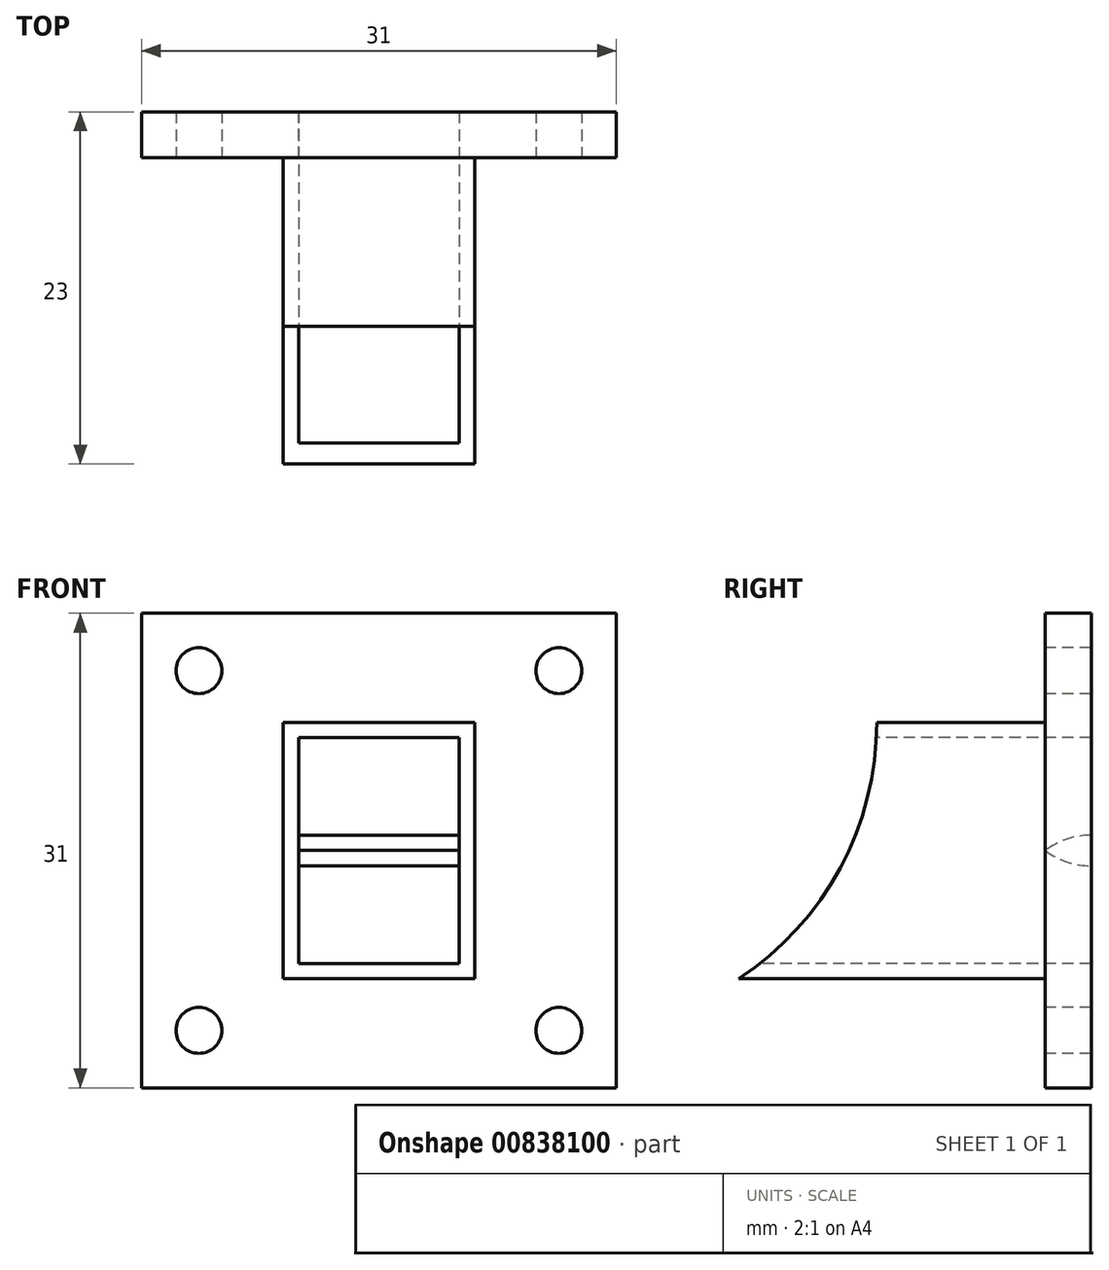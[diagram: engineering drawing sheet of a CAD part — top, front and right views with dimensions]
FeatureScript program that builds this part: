
annotation { "Feature Type Name" : "Feature", "Feature Type Description" : "" }
export const myFeature = defineFeature(function(context is Context, id is Id, definition is map)
    precondition{}
    {
        {
            var Q0;
            Q0=qCreatedBy(makeId("Front.planeOp"),FACE);
            var sketch = newSketch(context, id + "F0", { "sketchPlane" : qUnion([Q0])});
            skLineSegment(sketch, "E0.bottom", {"start": v(15.5, -15.5) * mm, "end": v(-15.5, -15.5) * mm});
            skLineSegment(sketch, "E0.top", {"start": v(15.5, 15.5) * mm, "end": v(-15.5, 15.5) * mm});
            skLineSegment(sketch, "E0.left", {"start": v(15.5, -15.5) * mm, "end": v(15.5, 15.5) * mm});
            skLineSegment(sketch, "E0.right", {"start": v(-15.5, -15.5) * mm, "end": v(-15.5, 15.5) * mm});
            skPoint(sketch, "E0.middle", {"position": v(0, 0) * mm});
            skSolve(sketch);
        }
        {
            var Q0;
            Q0 = qSketchRegion(id + "F0", true);
            extrude(context, id + "F1", {"entities" : qUnion([Q0]), "depth" : 3 * mm, "offsetDistance" : 25 * mm});
        }
        {
            var Q0;
            Q0=makeQuery(id+"F1.opExtrude","CAP_FACE",FACE,{"disambiguationData":[OSD([sQuery(id+"F0.wireOp",EDGE,"E0.bottom"),sQuery(id+"F0.wireOp",EDGE,"E0.top"),sQuery(id+"F0.wireOp",EDGE,"E0.left"),sQuery(id+"F0.wireOp",EDGE,"E0.right")])],"isStart":false});
            var sketch = newSketch(context, id + "F2", { "sketchPlane" : qUnion([Q0])});
            skCircle(sketch, "E1", {"center": v(-11.75, -11.75) * mm, "radius": 1.5 * mm});
            skCircle(sketch, "E2", {"center": v(-11.75, 11.75) * mm, "radius": 1.5 * mm});
            skCircle(sketch, "E3", {"center": v(11.75, 11.75) * mm, "radius": 1.5 * mm});
            skCircle(sketch, "E4", {"center": v(11.75, -11.75) * mm, "radius": 1.5 * mm});
            skLineSegment(sketch, "E5", {"start": v(-11.75, -11.75) * mm, "end": v(11.75, -11.75) * mm, "construction": true});
            skLineSegment(sketch, "E6", {"start": v(-11.75, 11.75) * mm, "end": v(-11.75, -11.75) * mm, "construction": true});
            skSolve(sketch);
        }
        {
            var Q0;
            Q0 = qSketchRegion(id + "F2", true);
            extrude(context, id + "F3", {"entities" : qUnion([Q0]), "operationType" : NewBodyOperationType.REMOVE, "oppositeDirection" : true, "depth" : 3 * mm, "offsetDistance" : 25 * mm});
        }
        {
            var Q0;
            Q0=makeQuery(id+"F1.opExtrude","CAP_FACE",FACE,{"disambiguationData":[OSD([sQuery(id+"F0.wireOp",EDGE,"E0.bottom"),sQuery(id+"F0.wireOp",EDGE,"E0.top"),sQuery(id+"F0.wireOp",EDGE,"E0.left"),sQuery(id+"F0.wireOp",EDGE,"E0.right")])],"isStart":false});
            var sketch = newSketch(context, id + "F4", { "sketchPlane" : qUnion([Q0])});
            skLineSegment(sketch, "E7.bottom", {"start": v(6.25, -8.37) * mm, "end": v(-6.25, -8.38) * mm});
            skLineSegment(sketch, "E7.top", {"start": v(6.25, 8.38) * mm, "end": v(-6.25, 8.38) * mm});
            skLineSegment(sketch, "E7.left", {"start": v(6.25, -8.37) * mm, "end": v(6.25, 8.38) * mm});
            skLineSegment(sketch, "E7.right", {"start": v(-6.25, -8.38) * mm, "end": v(-6.25, 8.38) * mm});
            skPoint(sketch, "E7.middle", {"position": v(0, 0) * mm});
            skSolve(sketch);
        }
        {
            var Q0;
            Q0 = qSketchRegion(id + "F4", true);
            extrude(context, id + "F5", {"entities" : qUnion([Q0]), "operationType" : NewBodyOperationType.ADD, "depth" : 20 * mm, "offsetDistance" : 25 * mm});
        }
        {
            var Q0;
            Q0=makeQuery(id+"F5.opExtrude","CAP_FACE",FACE,{"disambiguationData":[OSD([sQuery(id+"F4.wireOp",EDGE,"E7.bottom"),sQuery(id+"F4.wireOp",EDGE,"E7.top"),sQuery(id+"F4.wireOp",EDGE,"E7.left"),sQuery(id+"F4.wireOp",EDGE,"E7.right")])],"isStart":false});
            var sketch = newSketch(context, id + "F6", { "sketchPlane" : qUnion([Q0])});
            skLineSegment(sketch, "E8.bottom", {"start": v(5.25, -7.37) * mm, "end": v(-5.25, -7.38) * mm});
            skLineSegment(sketch, "E8.top", {"start": v(5.25, 7.38) * mm, "end": v(-5.25, 7.38) * mm});
            skLineSegment(sketch, "E8.left", {"start": v(5.25, -7.38) * mm, "end": v(5.25, 7.38) * mm});
            skLineSegment(sketch, "E8.right", {"start": v(-5.25, -7.38) * mm, "end": v(-5.25, 7.38) * mm});
            skPoint(sketch, "E8.middle", {"position": v(0, 0) * mm});
            skSolve(sketch);
        }
        {
            var Q0;
            Q0 = qSketchRegion(id + "F6", true);
            extrude(context, id + "F7", {"entities" : qUnion([Q0]), "operationType" : NewBodyOperationType.REMOVE, "oppositeDirection" : true, "depth" : 23 * mm, "offsetDistance" : 25 * mm});
        }
        {
            var Q0;
            Q0=makeQuery(id+"F5.opExtrude","SWEPT_FACE",FACE,{"disambiguationData":[OSD([sQuery(id+"F4.wireOp",EDGE,"E7.left")])]});
            var sketch = newSketch(context, id + "F8", { "sketchPlane" : qUnion([Q0])});
            skCircle(sketch, "E9", {"center": v(-34, 8.33) * mm, "radius": 20 * mm});
            skPoint(sketch, "E10", {"position": v(-23, -8.37) * mm});
            skSolve(sketch);
        }
        {
            var Q0;
            Q0 = qSketchRegion(id + "F8", true);
            extrude(context, id + "F9", {"entities" : qUnion([Q0]), "operationType" : NewBodyOperationType.REMOVE, "oppositeDirection" : true, "depth" : 25 * mm, "offsetDistance" : 25 * mm});
        }
        {
            var Q0;
            Q0=makeQuery(id+"F1.opExtrude","CAP_FACE",FACE,{"disambiguationData":[OSD([sQuery(id+"F0.wireOp",EDGE,"E0.bottom"),sQuery(id+"F0.wireOp",EDGE,"E0.top"),sQuery(id+"F0.wireOp",EDGE,"E0.left"),sQuery(id+"F0.wireOp",EDGE,"E0.right")])],"isStart":false});
            var sketch = newSketch(context, id + "F10", { "sketchPlane" : qUnion([Q0])});
            skLineSegment(sketch, "E11.bottom", {"start": v(6.25, -1) * mm, "end": v(-6.25, -1) * mm});
            skLineSegment(sketch, "E11.top", {"start": v(6.25, 0) * mm, "end": v(-6.25, 0) * mm});
            skLineSegment(sketch, "E11.left", {"start": v(6.25, -1) * mm, "end": v(6.25, 0) * mm});
            skLineSegment(sketch, "E11.right", {"start": v(-6.25, -1) * mm, "end": v(-6.25, 0) * mm});
            skPoint(sketch, "E11.middle", {"position": v(0, -0.5) * mm});
            skSolve(sketch);
        }
        {
            var Q0;
            Q0 = qSketchRegion(id + "F10", true);
            extrude(context, id + "F11", {"entities" : qUnion([Q0]), "operationType" : NewBodyOperationType.ADD, "oppositeDirection" : true, "depth" : 3 * mm, "offsetDistance" : 25 * mm});
        }
        {
            var Q0;
            Q0=makeQuery(id+"F11.opExtrude","CAP_EDGE",EDGE,{"disambiguationData":[OSD([sQuery(id+"F10.wireOp",EDGE,"E11.bottom")])],"isStart":true});
            fillet(context, id + "F12", {"entities" : qUnion([Q0]), "radius" : 5 * mm, "tangentPropagation" : true, "allowEdgeOverflow" : false});
        }
        {
            var Q0;
            Q0=makeQuery(id+"F1.opExtrude","CAP_FACE",FACE,{"disambiguationData":[OSD([sQuery(id+"F0.wireOp",EDGE,"E0.bottom"),sQuery(id+"F0.wireOp",EDGE,"E0.top"),sQuery(id+"F0.wireOp",EDGE,"E0.left"),sQuery(id+"F0.wireOp",EDGE,"E0.right")])],"isStart":false});
            var sketch = newSketch(context, id + "F13", { "sketchPlane" : qUnion([Q0])});
            skLineSegment(sketch, "E12.bottom", {"start": v(6.25, 1) * mm, "end": v(-6.25, 1) * mm});
            skLineSegment(sketch, "E12.top", {"start": v(6.25, 0) * mm, "end": v(-6.25, 0) * mm});
            skLineSegment(sketch, "E12.left", {"start": v(6.25, 1) * mm, "end": v(6.25, 0) * mm});
            skLineSegment(sketch, "E12.right", {"start": v(-6.25, 1) * mm, "end": v(-6.25, 0) * mm});
            skPoint(sketch, "E12.middle", {"position": v(0, 0.5) * mm});
            skSolve(sketch);
        }
        {
            var Q0;
            Q0 = qSketchRegion(id + "F13", true);
            extrude(context, id + "F14", {"entities" : qUnion([Q0]), "operationType" : NewBodyOperationType.ADD, "oppositeDirection" : true, "depth" : 3 * mm, "offsetDistance" : 25 * mm});
        }
        {
            var Q0;
            Q0=makeQuery(id+"F14.opExtrude","CAP_EDGE",EDGE,{"disambiguationData":[OSD([sQuery(id+"F13.wireOp",EDGE,"E12.bottom")])],"isStart":true});
            fillet(context, id + "F15", {"entities" : qUnion([Q0]), "radius" : 5 * mm, "tangentPropagation" : true, "allowEdgeOverflow" : false});
        }
    });
